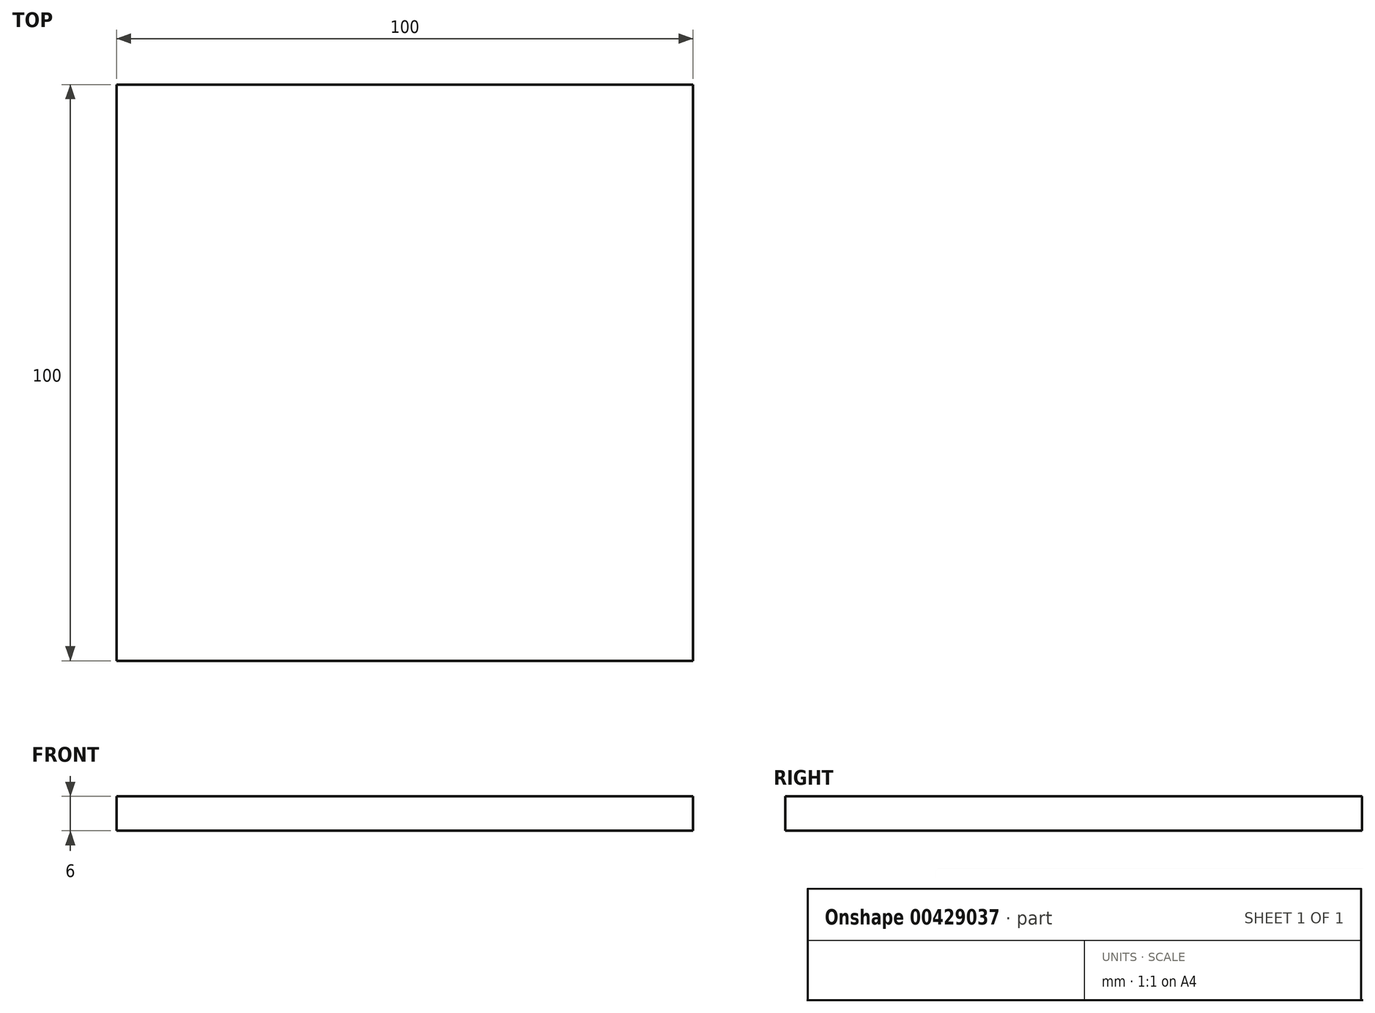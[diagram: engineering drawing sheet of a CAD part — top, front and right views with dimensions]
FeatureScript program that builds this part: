
annotation { "Feature Type Name" : "Feature", "Feature Type Description" : "" }
export const myFeature = defineFeature(function(context is Context, id is Id, definition is map)
    precondition{}
    {
        {
            var Q0;
            Q0=qCreatedBy(makeId("Top.planeOp"),FACE);
            var sketch = newSketch(context, id + "F0", { "sketchPlane" : qUnion([Q0])});
            skLineSegment(sketch, "E0.bottom", {"start": v(-44.83, 39.27) * mm, "end": v(55.17, 39.27) * mm});
            skLineSegment(sketch, "E0.top", {"start": v(-44.83, -60.73) * mm, "end": v(55.17, -60.73) * mm});
            skLineSegment(sketch, "E0.left", {"start": v(-44.83, 39.27) * mm, "end": v(-44.83, -60.73) * mm});
            skLineSegment(sketch, "E0.right", {"start": v(55.17, 39.27) * mm, "end": v(55.17, -60.73) * mm});
            skSolve(sketch);
        }
        {
            var Q0;
            Q0=makeQuery(id+"F0.imprint","IMPRINT",FACE,{"disambiguationData":[TD([[makeQuery(id+"F0.imprint","IMPRINT",EDGE,{"derivedFrom":sQuery(id+"F0.wireOp",EDGE,"E0.bottom")}),-1.0]])]});
            extrude(context, id + "F1", {"entities" : qUnion([Q0]), "depth" : 6 * mm});
        }
    });
